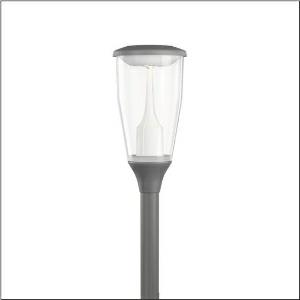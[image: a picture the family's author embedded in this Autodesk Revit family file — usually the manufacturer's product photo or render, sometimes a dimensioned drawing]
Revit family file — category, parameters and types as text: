
# Revit family: dl_11_iq___st1_2a_5xa5565ef14hp00022_07bc
name_source: partatom
category: Lighting Fixtures
units: mm (PartAtom-declared; Revit-internal decimal feet)

## family parameters
Cut with Voids When Loaded = No
Host = Face
Light Source = No
Part Type = Normal
Room Calculation Point = No
Round Connector Dimension = Use Diameter
Shared = No

## types (1)
- --- (1 x LED, 4840 lm, 33.6 W, 3000K)
    Apparent Load = 34 VA
    CIE Flux Codes = 23 60 93 95 100
    Color Rendering = 70
    Color Temperature = 3000K
    Default Elevation = 1800 mm
    Description = DL 11 iQ, mast luminaire, Module 540 iQ-SR, primary light control with 3 zone facetted reflector, of plastic, silver coated, highly specular, structured, primary optical cover: cover, of PMMA, transparent, light distribution: ST1.2a, light emission: direct distribution, primary light characteristic: asymmetric, installation type: post-top, LED, High Power LED, rated luminous flux: 0lm, luminous efficacy: 144lm/W, light colour: 730, colour temperature: 3000K, control gear: iQ Street-Remote, control: Street-Remote, Auto-Match, Temp-Guard, Lumen-Switch, Night-Set, Smart-Wire, Light-Fading, Desk-Remote (wireless, voltage-free reading and setting of iQ features in the workshop via application-optimized NFC function/RFID function), optimised constant luminous flux control (CLO 2.0), mains connection: 220..240V, AC, 50/60Hz, connection cable pre-assembled, cable length: 5,5m, wiring characteristics: H07RN-F, 5-core, 1.5mm², start of lifetime: 0W, end of service life: 0W, reduction: 15W, luminaire housing, upper part, of diecast aluminium, coated, SITECO metallic grey (DB 702S), spigot size: 60mm (post-top), mounting height: 3..5m, post-top mast mounting element, of diecast aluminium, coated, SITECO metallic grey (DB 702S), Module 540 iQ-SR, traffic white (RAL 9016), equipment: Power, protection rating (complete): IP66, insulation class (complete): insulation class II (safety insulation), certification: CE, ENEC, ENEC+, VDE, impact resistance: IK07, packaging unit: 1 piece

Light Distribution: ST1.2a
    Height = 665 mm
    Lamp = 1 x LED
    Lamp Light Flux = 4840 lm
    Lamp Power = 33.6 W
    Lamp count = 1
    Length = 334 mm
    Luminous efficacy = 144 lm/W
    Manufacturer = Siteco
    ModVariant = No
    Model = 5XA5565EF14HP00022
    Number of Poles = 1
    OnlyDefault = Yes
    Power Factor = 1
    Product Name = DL 11 iQ | ST1.2a
    Product group = mast luminaire | pylon top
    ProductGroupID = 6100
    Protection Class = Protection class II
    Protection Degree = IP 66
    RLX_Detail_Level = 1
    RLX_Emergency_Light_Flux = 0 lm
    RLX_Emergency_Type = 0
    RLX_Emergency_Type_DB = No
    RlxData = <blob elided: 156161 chars, md5=b1ba30e3>
    Socket = socket
    Standby Power = 0 W
    System Light Flux = 4840 lm
    System Power = 34 W
    Type Comments = factory setting: luminous flux: 100 % | dim-lin: 254 | 695 mA
    Type Image = l_1258354.jpg
    URL = http://relux.com
    VarID = @adj_040311
    Voltage = 0 V
    Weight = 0.00 kg
    Width = 0 mm  [stored 0 ft]

note: [stored X ft] marks values corroborated as IEEE doubles in the binary element streams (Revit-internal decimal feet)

## geometry (parser evidence)
native form markers: Blend x4, Sweep x9
no freeform markers — native parametric forms only
